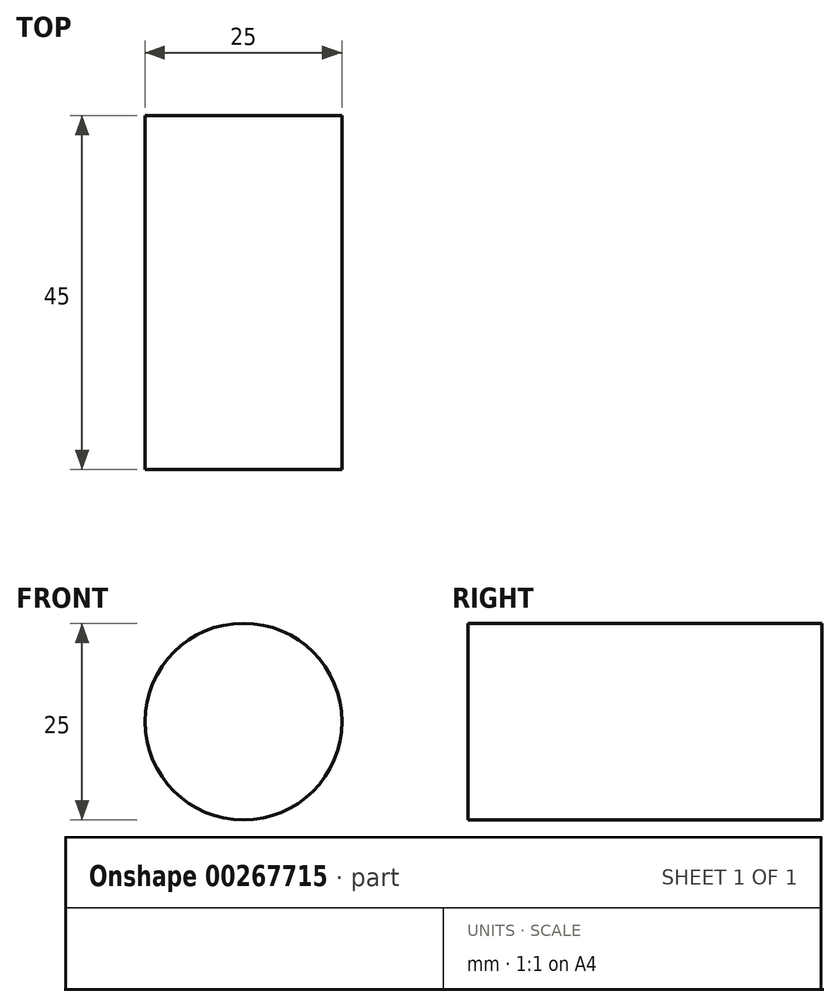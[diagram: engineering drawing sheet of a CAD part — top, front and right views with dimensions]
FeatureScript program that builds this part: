
annotation { "Feature Type Name" : "Feature", "Feature Type Description" : "" }
export const myFeature = defineFeature(function(context is Context, id is Id, definition is map)
    precondition{}
    {
        {
            var Q0;
            Q0=qCreatedBy(makeId("Front.planeOp"),FACE);
            var sketch = newSketch(context, id + "F0", { "sketchPlane" : qUnion([Q0])});
            skCircle(sketch, "E0", {"center": v(0, 0) * mm, "radius": 12.5 * mm});
            skSolve(sketch);
        }
        {
            var Q0;
            Q0=makeQuery(id+"F0.imprint","IMPRINT",FACE,{"disambiguationData":[TD([[makeQuery(id+"F0.imprint","IMPRINT",EDGE,{"derivedFrom":sQuery(id+"F0.wireOp",EDGE,"E0")}),1.0]])]});
            extrude(context, id + "F1", {"entities" : qUnion([Q0]), "oppositeDirection" : true, "depth" : 45 * mm});
        }
    });
